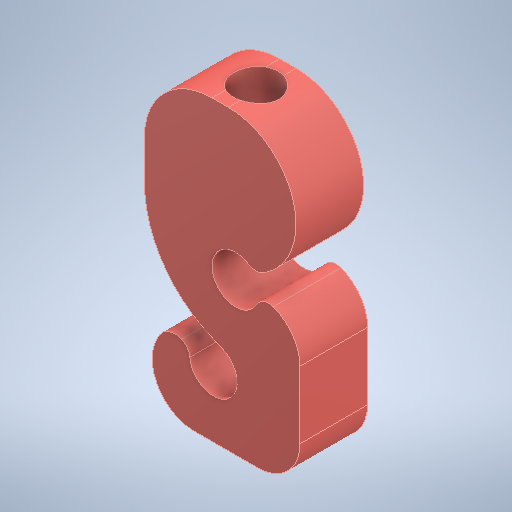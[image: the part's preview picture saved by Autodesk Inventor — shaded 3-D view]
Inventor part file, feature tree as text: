
AUTODESK INVENTOR PART (.ipt)
format: ipt  version: 2025.2 (Build 292293000, 293)  size: 313,856 bytes
history: native  units: in
note: dims shown in document units (in); Inventor stores cm internally (conversion verified against a paired STEP export)
features: fillet x5, extrude x1, sketch x1, other x1
ambient origin geometry x8: Origin, YZ Plane, XZ Plane, XY Plane, X Axis, Y Axis, Z Axis, Center Point
bodies: Solid1 (feature_tree)
feature tree (8):
  extrude  "Extrusion1"  Depth=0.0787in
  fillet  "Fillet1"  Radius=0.3937in
  fillet  "Fillet2"  Radius=0.0394in
  fillet  "Fillet3"  Radius=0.0394in
  fillet  "Fillet4"  Radius=0.0394in
  fillet  "Fillet5"  Radius=0.0394in
  sketch  "Sketch1"  dims[d0=0.1378in d1=0.1378in d2=0.3937in d3=0.0in d4=0.0394in d5=0.0394in d6=0.0394in d7=0.0394in d8=0.0787in d9=0.0in d10=0.0in d11=0.0in]
  other  "JAdapter"
